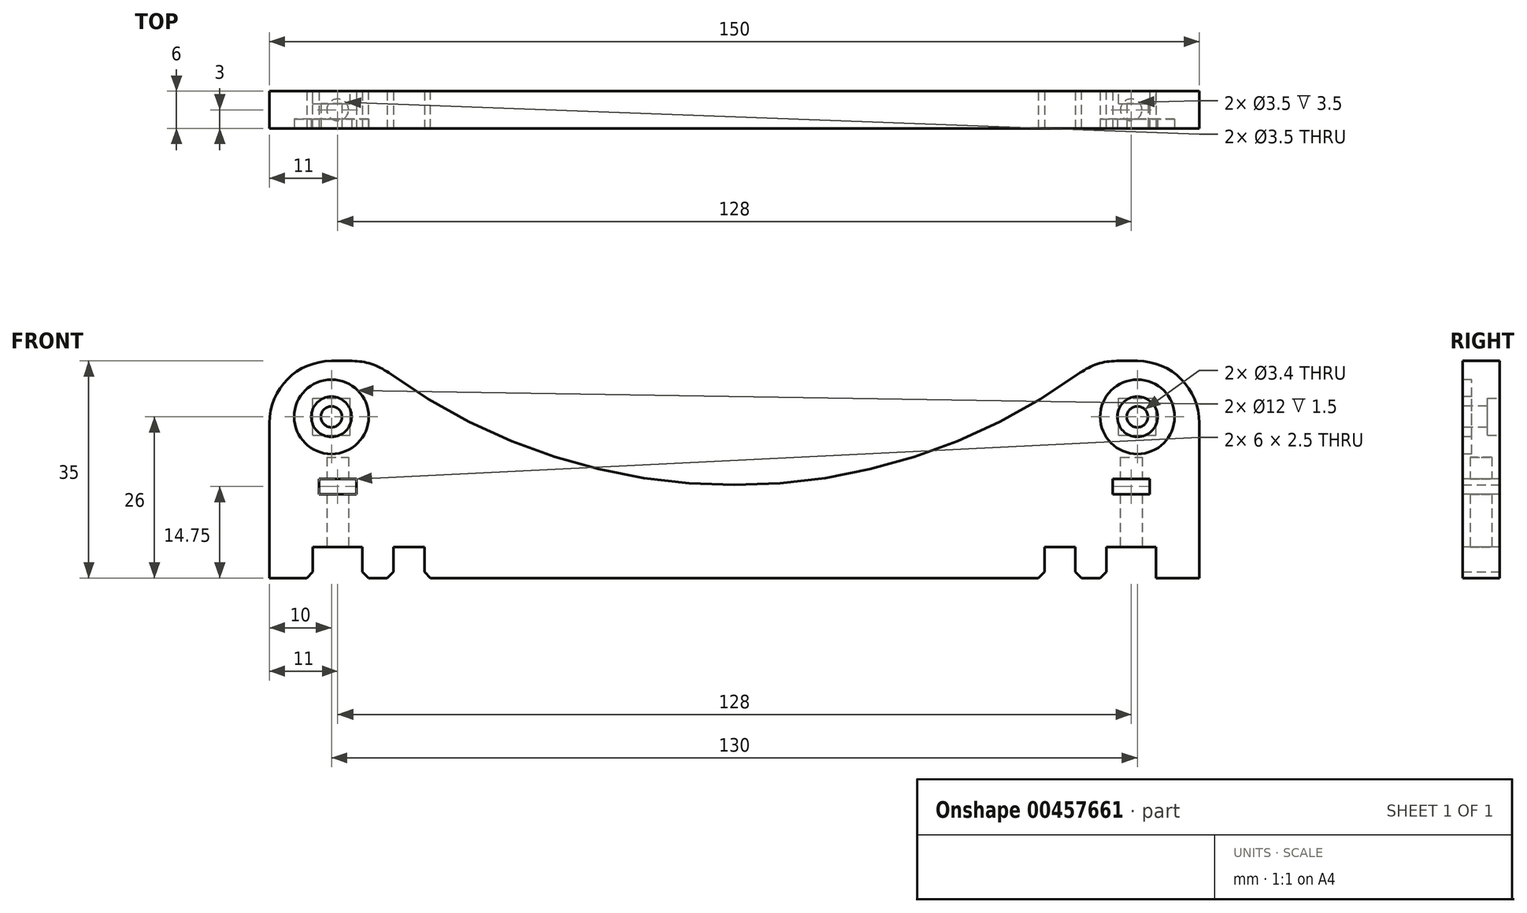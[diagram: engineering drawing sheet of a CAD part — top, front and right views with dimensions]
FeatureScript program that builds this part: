
annotation { "Feature Type Name" : "Feature", "Feature Type Description" : "" }
export const myFeature = defineFeature(function(context is Context, id is Id, definition is map)
    precondition{}
    {
        {
            var Q0;
            Q0=qCreatedBy(makeId("Front.planeOp"),FACE);
            var sketch = newSketch(context, id + "F0", { "sketchPlane" : qUnion([Q0])});
            skLineSegment(sketch, "E0.bottom", {"start": v(75, 0) * mm, "end": v(-75, 0) * mm});
            skLineSegment(sketch, "E0.top", {"start": v(75, 35) * mm, "end": v(-75, 35) * mm});
            skLineSegment(sketch, "E0.left", {"start": v(75, 0) * mm, "end": v(75, 35) * mm});
            skLineSegment(sketch, "E0.right", {"start": v(-75, 0) * mm, "end": v(-75, 35) * mm});
            skPoint(sketch, "E0.middle", {"position": v(0, 10) * mm});
            skCircle(sketch, "E1", {"center": v(0, 110) * mm, "radius": 100 * mm, "construction": true});
            skCircle(sketch, "E2", {"center": v(0, 110) * mm, "radius": 95 * mm});
            skSolve(sketch);
        }
        {
            var Q0;
            Q0=makeQuery(id+"F0.imprint","IMPRINT",FACE,{"disambiguationData":[TD([[makeQuery(id+"F0.imprint","IMPRINT",EDGE,{"derivedFrom":sQuery(id+"F0.wireOp",EDGE,"E0.bottom")}),-1.0]])]});
            extrude(context, id + "F1", {"entities" : qUnion([Q0]), "depth" : 6 * mm});
        }
        {
            var Q0;
            Q0=makeQuery(id+"F1.opExtrude","CAP_FACE",FACE,{"disambiguationData":[OSD([sQuery(id+"F0.wireOp",EDGE,"E0.bottom"),sQuery(id+"F0.wireOp",EDGE,"E0.top"),sQuery(id+"F0.wireOp",EDGE,"E0.left"),sQuery(id+"F0.wireOp",EDGE,"E0.right"),sQuery(id+"F0.wireOp",EDGE,"E2")])],"isStart":false});
            var sketch = newSketch(context, id + "F2", { "sketchPlane" : qUnion([Q0])});
            skCircle(sketch, "E3", {"center": v(0, 110) * mm, "radius": 100 * mm, "construction": true});
            skCircle(sketch, "E4", {"center": v(-65, 26) * mm, "radius": 6 * mm});
            skCircle(sketch, "E5", {"center": v(65, 26) * mm, "radius": 6 * mm});
            skCircle(sketch, "E6", {"center": v(-65, 26) * mm, "radius": 3.25 * mm});
            skCircle(sketch, "E7", {"center": v(65, 26) * mm, "radius": 3.25 * mm});
            skSolve(sketch);
        }
        {
            var Q0;
            Q0=makeQuery(id+"F2.imprint","IMPRINT",FACE,{"disambiguationData":[TD([[makeQuery(id+"F2.imprint","IMPRINT",EDGE,{"derivedFrom":sQuery(id+"F2.wireOp",EDGE,"E4")}),1.0]])]});
            var Q1;
            Q1=makeQuery(id+"F2.imprint","IMPRINT",FACE,{"disambiguationData":[TD([[makeQuery(id+"F2.imprint","IMPRINT",EDGE,{"derivedFrom":sQuery(id+"F2.wireOp",EDGE,"E5")}),1.0]])]});
            extrude(context, id + "F3", {"entities" : qUnion([Q0, Q1]), "operationType" : NewBodyOperationType.REMOVE, "oppositeDirection" : true, "depth" : 1.5 * mm});
        }
        {
            var Q0;
            {var subQ0=sQuery(id+"F0.wireOp",EDGE,"E0.right");var subQ1=sQuery(id+"F0.wireOp",EDGE,"E0.top");var subQ2=sQuery(id+"F0.wireOp",EDGE,"E2");var subQ3=sQuery(id+"F0.wireOp",EDGE,"E0.left");var subQ4=sQuery(id+"F0.wireOp",EDGE,"E0.bottom");Q0=makeQuery(id+"F3.boolean.opBoolean","SPLIT",FACE,{"disambiguationData":[TD([makeQuery(id+"F1.opExtrude","SWEPT_FACE",FACE,{"disambiguationData":[OSD([subQ4])]})])],"derivedFrom":makeQuery(id+"F1.opExtrude","CAP_FACE",FACE,{"disambiguationData":[OSD([subQ4,subQ1,subQ3,subQ0,subQ2])],"isStart":false})});}
            var sketch = newSketch(context, id + "F4", { "sketchPlane" : qUnion([Q0])});
            skLineSegment(sketch, "E8.bottom", {"start": v(-68, 0) * mm, "end": v(-60, 0) * mm});
            skLineSegment(sketch, "E8.top", {"start": v(-68, 5) * mm, "end": v(-60, 5) * mm});
            skLineSegment(sketch, "E8.left", {"start": v(-68, 0) * mm, "end": v(-68, 5) * mm});
            skLineSegment(sketch, "E8.right", {"start": v(-60, 0) * mm, "end": v(-60, 5) * mm});
            skLineSegment(sketch, "E9.bottom", {"start": v(60, 0) * mm, "end": v(68, 0) * mm});
            skLineSegment(sketch, "E9.top", {"start": v(60, 5) * mm, "end": v(68, 5) * mm});
            skLineSegment(sketch, "E9.left", {"start": v(60, 0) * mm, "end": v(60, 5) * mm});
            skLineSegment(sketch, "E9.right", {"start": v(68, 0) * mm, "end": v(68, 5) * mm});
            skLineSegment(sketch, "E10.bottom", {"start": v(-67, 13.5) * mm, "end": v(-61, 13.5) * mm});
            skLineSegment(sketch, "E10.top", {"start": v(-67, 16) * mm, "end": v(-61, 16) * mm});
            skLineSegment(sketch, "E10.left", {"start": v(-67, 13.5) * mm, "end": v(-67, 16) * mm});
            skLineSegment(sketch, "E10.right", {"start": v(-61, 13.5) * mm, "end": v(-61, 16) * mm});
            skLineSegment(sketch, "E11.bottom", {"start": v(61, 16) * mm, "end": v(67, 16) * mm});
            skLineSegment(sketch, "E11.top", {"start": v(61, 13.5) * mm, "end": v(67, 13.5) * mm});
            skLineSegment(sketch, "E11.left", {"start": v(61, 16) * mm, "end": v(61, 13.5) * mm});
            skLineSegment(sketch, "E11.right", {"start": v(67, 16) * mm, "end": v(67, 13.5) * mm});
            skLineSegment(sketch, "E12.bottom", {"start": v(-55, 5) * mm, "end": v(-50, 5) * mm});
            skLineSegment(sketch, "E12.top", {"start": v(-55, 0) * mm, "end": v(-50, 0) * mm});
            skLineSegment(sketch, "E12.left", {"start": v(-55, 5) * mm, "end": v(-55, 0) * mm});
            skLineSegment(sketch, "E12.right", {"start": v(-50, 5) * mm, "end": v(-50, 0) * mm});
            skLineSegment(sketch, "E13.bottom", {"start": v(55, 0) * mm, "end": v(50, 0) * mm});
            skLineSegment(sketch, "E13.top", {"start": v(55, 5) * mm, "end": v(50, 5) * mm});
            skLineSegment(sketch, "E13.left", {"start": v(55, 0) * mm, "end": v(55, 5) * mm});
            skLineSegment(sketch, "E13.right", {"start": v(50, 0) * mm, "end": v(50, 5) * mm});
            skSolve(sketch);
        }
        {
            var Q0;
            Q0=makeQuery(id+"F4.imprint","IMPRINT",FACE,{"disambiguationData":[TD([[makeQuery(id+"F4.imprint","IMPRINT",EDGE,{"derivedFrom":sQuery(id+"F4.wireOp",EDGE,"E8.bottom")}),-1.0]])]});
            var Q1;
            Q1=makeQuery(id+"F4.imprint","IMPRINT",FACE,{"disambiguationData":[TD([[makeQuery(id+"F4.imprint","IMPRINT",EDGE,{"derivedFrom":sQuery(id+"F4.wireOp",EDGE,"E9.bottom")}),-1.0]])]});
            var Q2;
            Q2=makeQuery(id+"F4.imprint","IMPRINT",FACE,{"disambiguationData":[TD([[makeQuery(id+"F4.imprint","IMPRINT",EDGE,{"derivedFrom":sQuery(id+"F4.wireOp",EDGE,"E10.bottom")}),1.0]])]});
            var Q3;
            Q3=makeQuery(id+"F4.imprint","IMPRINT",FACE,{"disambiguationData":[TD([[makeQuery(id+"F4.imprint","IMPRINT",EDGE,{"derivedFrom":sQuery(id+"F4.wireOp",EDGE,"E11.bottom")}),-1.0]])]});
            var Q4;
            Q4=makeQuery(id+"F4.imprint","IMPRINT",FACE,{"disambiguationData":[TD([[makeQuery(id+"F4.imprint","IMPRINT",EDGE,{"derivedFrom":sQuery(id+"F4.wireOp",EDGE,"E12.bottom")}),-1.0]])]});
            var Q5;
            Q5=makeQuery(id+"F4.imprint","IMPRINT",FACE,{"disambiguationData":[TD([[makeQuery(id+"F4.imprint","IMPRINT",EDGE,{"derivedFrom":sQuery(id+"F4.wireOp",EDGE,"E13.bottom")}),-1.0]])]});
            extrude(context, id + "F5", {"entities" : qUnion([Q0, Q1, Q2, Q3, Q4, Q5]), "operationType" : NewBodyOperationType.REMOVE, "endBound" : BoundingType.THROUGH_ALL, "oppositeDirection" : true, "depth" : 25 * mm});
        }
        {
            var Q0;
            Q0=makeQuery(id+"F1.opExtrude","SWEPT_EDGE",EDGE,{"disambiguationData":[OSD([sQuery(id+"F0.wireOp",EDGE,"E0.top"),sQuery(id+"F0.wireOp",EDGE,"E0.right")])]});
            var Q1;
            Q1=makeQuery(id+"F1.opExtrude","SWEPT_EDGE",EDGE,{"disambiguationData":[OSD([sQuery(id+"F0.wireOp",EDGE,"E0.top"),sQuery(id+"F0.wireOp",EDGE,"E0.left")])]});
            var Q2;
            {var subQ0=sQuery(id+"F0.wireOp",EDGE,"E2");var subQ1=sQuery(id+"F0.wireOp",EDGE,"E0.top");Q2=makeQuery(id+"F1.opExtrude","SWEPT_EDGE",EDGE,{"disambiguationData":[OSD([subQ1,subQ0]),TDD([makeQuery(id+"F0.imprint","INTERSECT",VERTEX,{"disambiguationData":[OD(0.0)],"derivedFrom":[subQ1,subQ0]})])]});}
            var Q3;
            {var subQ0=sQuery(id+"F0.wireOp",EDGE,"E2");var subQ1=sQuery(id+"F0.wireOp",EDGE,"E0.top");Q3=makeQuery(id+"F1.opExtrude","SWEPT_EDGE",EDGE,{"disambiguationData":[OSD([subQ1,subQ0]),TDD([makeQuery(id+"F0.imprint","INTERSECT",VERTEX,{"disambiguationData":[OD(1.0)],"derivedFrom":[subQ1,subQ0]})])]});}
            fillet(context, id + "F6", {"entities" : qUnion([Q0, Q1, Q2, Q3]), "radius" : 10 * mm, "tangentPropagation" : true, "allowEdgeOverflow" : false});
        }
        {
            var Q0;
            Q0=makeQuery(id+"F5.boolean.opBoolean","COPY",EDGE,{"derivedFrom":makeQuery(id+"F5.opExtrude","SWEPT_EDGE",EDGE,{"disambiguationData":[OSD([sQuery(id+"F0.wireOp",EDGE,"E0.bottom"),sQuery(id+"F4.wireOp",EDGE,"E8.bottom"),sQuery(id+"F4.wireOp",EDGE,"E8.left")])]})});
            var Q1;
            Q1=makeQuery(id+"F5.boolean.opBoolean","COPY",EDGE,{"derivedFrom":makeQuery(id+"F5.opExtrude","SWEPT_EDGE",EDGE,{"disambiguationData":[OSD([sQuery(id+"F0.wireOp",EDGE,"E0.bottom"),sQuery(id+"F4.wireOp",EDGE,"E8.bottom"),sQuery(id+"F4.wireOp",EDGE,"E8.right")])]})});
            var Q2;
            Q2=makeQuery(id+"F5.boolean.opBoolean","COPY",EDGE,{"derivedFrom":makeQuery(id+"F5.opExtrude","SWEPT_EDGE",EDGE,{"disambiguationData":[OSD([sQuery(id+"F0.wireOp",EDGE,"E0.bottom"),sQuery(id+"F4.wireOp",EDGE,"E9.bottom"),sQuery(id+"F4.wireOp",EDGE,"E9.left")])]})});
            var Q3;
            Q3=makeQuery(id+"F5.boolean.opBoolean","COPY",EDGE,{"derivedFrom":makeQuery(id+"F5.opExtrude","SWEPT_EDGE",EDGE,{"disambiguationData":[OSD([sQuery(id+"F0.wireOp",EDGE,"E0.bottom"),sQuery(id+"F4.wireOp",EDGE,"E9.bottom"),sQuery(id+"F4.wireOp",EDGE,"E9.right")])]})});
            var Q4;
            Q4=makeQuery(id+"F5.boolean.opBoolean","COPY",EDGE,{"derivedFrom":makeQuery(id+"F5.opExtrude","SWEPT_EDGE",EDGE,{"disambiguationData":[OSD([sQuery(id+"F0.wireOp",EDGE,"E0.bottom"),sQuery(id+"F4.wireOp",EDGE,"E12.top"),sQuery(id+"F4.wireOp",EDGE,"E12.left")])]})});
            var Q5;
            Q5=makeQuery(id+"F5.boolean.opBoolean","COPY",EDGE,{"derivedFrom":makeQuery(id+"F5.opExtrude","SWEPT_EDGE",EDGE,{"disambiguationData":[OSD([sQuery(id+"F0.wireOp",EDGE,"E0.bottom"),sQuery(id+"F4.wireOp",EDGE,"E12.top"),sQuery(id+"F4.wireOp",EDGE,"E12.right")])]})});
            var Q6;
            Q6=makeQuery(id+"F5.boolean.opBoolean","COPY",EDGE,{"derivedFrom":makeQuery(id+"F5.opExtrude","SWEPT_EDGE",EDGE,{"disambiguationData":[OSD([sQuery(id+"F0.wireOp",EDGE,"E0.bottom"),sQuery(id+"F4.wireOp",EDGE,"E13.bottom"),sQuery(id+"F4.wireOp",EDGE,"E13.right")])]})});
            var Q7;
            Q7=makeQuery(id+"F5.boolean.opBoolean","COPY",EDGE,{"derivedFrom":makeQuery(id+"F5.opExtrude","SWEPT_EDGE",EDGE,{"disambiguationData":[OSD([sQuery(id+"F0.wireOp",EDGE,"E0.bottom"),sQuery(id+"F4.wireOp",EDGE,"E13.bottom"),sQuery(id+"F4.wireOp",EDGE,"E13.left")])]})});
            chamfer(context, id + "F7", {"entities" : qUnion([Q0, Q1, Q2, Q3, Q4, Q5, Q6, Q7]), "width" : 1 * mm, "tangentPropagation" : true});
        }
        {
            var Q0;
            Q0=makeQuery(id+"F5.boolean.opBoolean","COPY",FACE,{"derivedFrom":makeQuery(id+"F5.opExtrude","SWEPT_FACE",FACE,{"disambiguationData":[OSD([sQuery(id+"F4.wireOp",EDGE,"E8.top")])]})});
            var sketch = newSketch(context, id + "F8", { "sketchPlane" : qUnion([Q0])});
            skCircle(sketch, "E14", {"center": v(-64, 3) * mm, "radius": 1.75 * mm});
            skSolve(sketch);
        }
        {
            var Q0;
            Q0=makeQuery(id+"F8.imprint","IMPRINT",FACE,{"disambiguationData":[TD([[makeQuery(id+"F8.imprint","IMPRINT",EDGE,{"derivedFrom":sQuery(id+"F8.wireOp",EDGE,"E14")}),1.0]])]});
            extrude(context, id + "F9", {"entities" : qUnion([Q0]), "operationType" : NewBodyOperationType.REMOVE, "oppositeDirection" : true, "depth" : 14.5 * mm});
        }
        {
            var Q0;
            Q0=makeQuery(id+"F5.boolean.opBoolean","COPY",FACE,{"derivedFrom":makeQuery(id+"F5.opExtrude","SWEPT_FACE",FACE,{"disambiguationData":[OSD([sQuery(id+"F4.wireOp",EDGE,"E9.top")])]})});
            var sketch = newSketch(context, id + "F10", { "sketchPlane" : qUnion([Q0])});
            skCircle(sketch, "E15", {"center": v(64, 3) * mm, "radius": 1.75 * mm});
            skSolve(sketch);
        }
        {
            var Q0;
            Q0=makeQuery(id+"F10.imprint","IMPRINT",FACE,{"disambiguationData":[TD([[makeQuery(id+"F10.imprint","IMPRINT",EDGE,{"derivedFrom":sQuery(id+"F10.wireOp",EDGE,"E15")}),1.0]])]});
            extrude(context, id + "F11", {"entities" : qUnion([Q0]), "operationType" : NewBodyOperationType.REMOVE, "oppositeDirection" : true, "depth" : 14.5 * mm});
        }
        {
            var Q0;
            Q0=makeQuery(id+"F3.boolean.opBoolean","SPLIT",FACE,{"disambiguationData":[TD([makeQuery(id+"F3.opExtrude","SWEPT_FACE",FACE,{"disambiguationData":[OSD([sQuery(id+"F2.wireOp",EDGE,"E6")])]})])],"derivedFrom":makeQuery(id+"F1.opExtrude","CAP_FACE",FACE,{"disambiguationData":[OSD([sQuery(id+"F0.wireOp",EDGE,"E0.bottom"),sQuery(id+"F0.wireOp",EDGE,"E0.top"),sQuery(id+"F0.wireOp",EDGE,"E0.left"),sQuery(id+"F0.wireOp",EDGE,"E0.right"),sQuery(id+"F0.wireOp",EDGE,"E2")])],"isStart":false})});
            var sketch = newSketch(context, id + "F12", { "sketchPlane" : qUnion([Q0])});
            skCircle(sketch, "E16", {"center": v(-65, 26) * mm, "radius": 1.7 * mm});
            skSolve(sketch);
        }
        {
            var Q0;
            Q0=makeQuery(id+"F12.imprint","IMPRINT",FACE,{"disambiguationData":[TD([[makeQuery(id+"F12.imprint","IMPRINT",EDGE,{"derivedFrom":sQuery(id+"F12.wireOp",EDGE,"E16")}),1.0]])]});
            extrude(context, id + "F13", {"entities" : qUnion([Q0]), "operationType" : NewBodyOperationType.REMOVE, "endBound" : BoundingType.THROUGH_ALL, "oppositeDirection" : true, "depth" : 25 * mm});
        }
        {
            var Q0;
            Q0=makeQuery(id+"F3.boolean.opBoolean","SPLIT",FACE,{"disambiguationData":[TD([makeQuery(id+"F3.opExtrude","SWEPT_FACE",FACE,{"disambiguationData":[OSD([sQuery(id+"F2.wireOp",EDGE,"E7")])]})])],"derivedFrom":makeQuery(id+"F1.opExtrude","CAP_FACE",FACE,{"disambiguationData":[OSD([sQuery(id+"F0.wireOp",EDGE,"E0.bottom"),sQuery(id+"F0.wireOp",EDGE,"E0.top"),sQuery(id+"F0.wireOp",EDGE,"E0.left"),sQuery(id+"F0.wireOp",EDGE,"E0.right"),sQuery(id+"F0.wireOp",EDGE,"E2")])],"isStart":false})});
            var sketch = newSketch(context, id + "F14", { "sketchPlane" : qUnion([Q0])});
            skCircle(sketch, "E17", {"center": v(65, 26) * mm, "radius": 1.7 * mm});
            skSolve(sketch);
        }
        {
            var Q0;
            Q0=makeQuery(id+"F14.imprint","IMPRINT",FACE,{"disambiguationData":[TD([[makeQuery(id+"F14.imprint","IMPRINT",EDGE,{"derivedFrom":sQuery(id+"F14.wireOp",EDGE,"E17")}),1.0]])]});
            extrude(context, id + "F15", {"entities" : qUnion([Q0]), "operationType" : NewBodyOperationType.REMOVE, "endBound" : BoundingType.THROUGH_ALL, "oppositeDirection" : true, "depth" : 25 * mm});
        }
        {
            var Q0;
            Q0=makeQuery(id+"F1.opExtrude","CAP_FACE",FACE,{"disambiguationData":[OSD([sQuery(id+"F0.wireOp",EDGE,"E0.bottom"),sQuery(id+"F0.wireOp",EDGE,"E0.top"),sQuery(id+"F0.wireOp",EDGE,"E0.left"),sQuery(id+"F0.wireOp",EDGE,"E0.right"),sQuery(id+"F0.wireOp",EDGE,"E2")])],"isStart":true});
            var sketch = newSketch(context, id + "F16", { "sketchPlane" : qUnion([Q0])});
            skLineSegment(sketch, "E18.bottom", {"start": v(-62, 23) * mm, "end": v(-68, 23) * mm});
            skLineSegment(sketch, "E18.top", {"start": v(-62, 29) * mm, "end": v(-68, 29) * mm});
            skLineSegment(sketch, "E18.left", {"start": v(-62, 23) * mm, "end": v(-62, 29) * mm});
            skLineSegment(sketch, "E18.right", {"start": v(-68, 23) * mm, "end": v(-68, 29) * mm});
            skPoint(sketch, "E18.middle", {"position": v(-65, 26) * mm});
            skLineSegment(sketch, "E19.bottom", {"start": v(68, 23) * mm, "end": v(62, 23) * mm});
            skLineSegment(sketch, "E19.top", {"start": v(68, 29) * mm, "end": v(62, 29) * mm});
            skLineSegment(sketch, "E19.left", {"start": v(68, 23) * mm, "end": v(68, 29) * mm});
            skLineSegment(sketch, "E19.right", {"start": v(62, 23) * mm, "end": v(62, 29) * mm});
            skPoint(sketch, "E19.middle", {"position": v(65, 26) * mm});
            skSolve(sketch);
        }
        {
            var Q0;
            Q0=makeQuery(id+"F16.imprint","IMPRINT",FACE,{"disambiguationData":[TD([[makeQuery(id+"F16.imprint","IMPRINT",EDGE,{"derivedFrom":sQuery(id+"F16.wireOp",EDGE,"E19.bottom")}),-1.0]])]});
            var Q1;
            Q1=makeQuery(id+"F16.imprint","IMPRINT",FACE,{"disambiguationData":[TD([[makeQuery(id+"F16.imprint","IMPRINT",EDGE,{"derivedFrom":sQuery(id+"F16.wireOp",EDGE,"E18.bottom")}),-1.0]])]});
            extrude(context, id + "F17", {"entities" : qUnion([Q0, Q1]), "operationType" : NewBodyOperationType.REMOVE, "oppositeDirection" : true, "depth" : 2 * mm});
        }
    });
